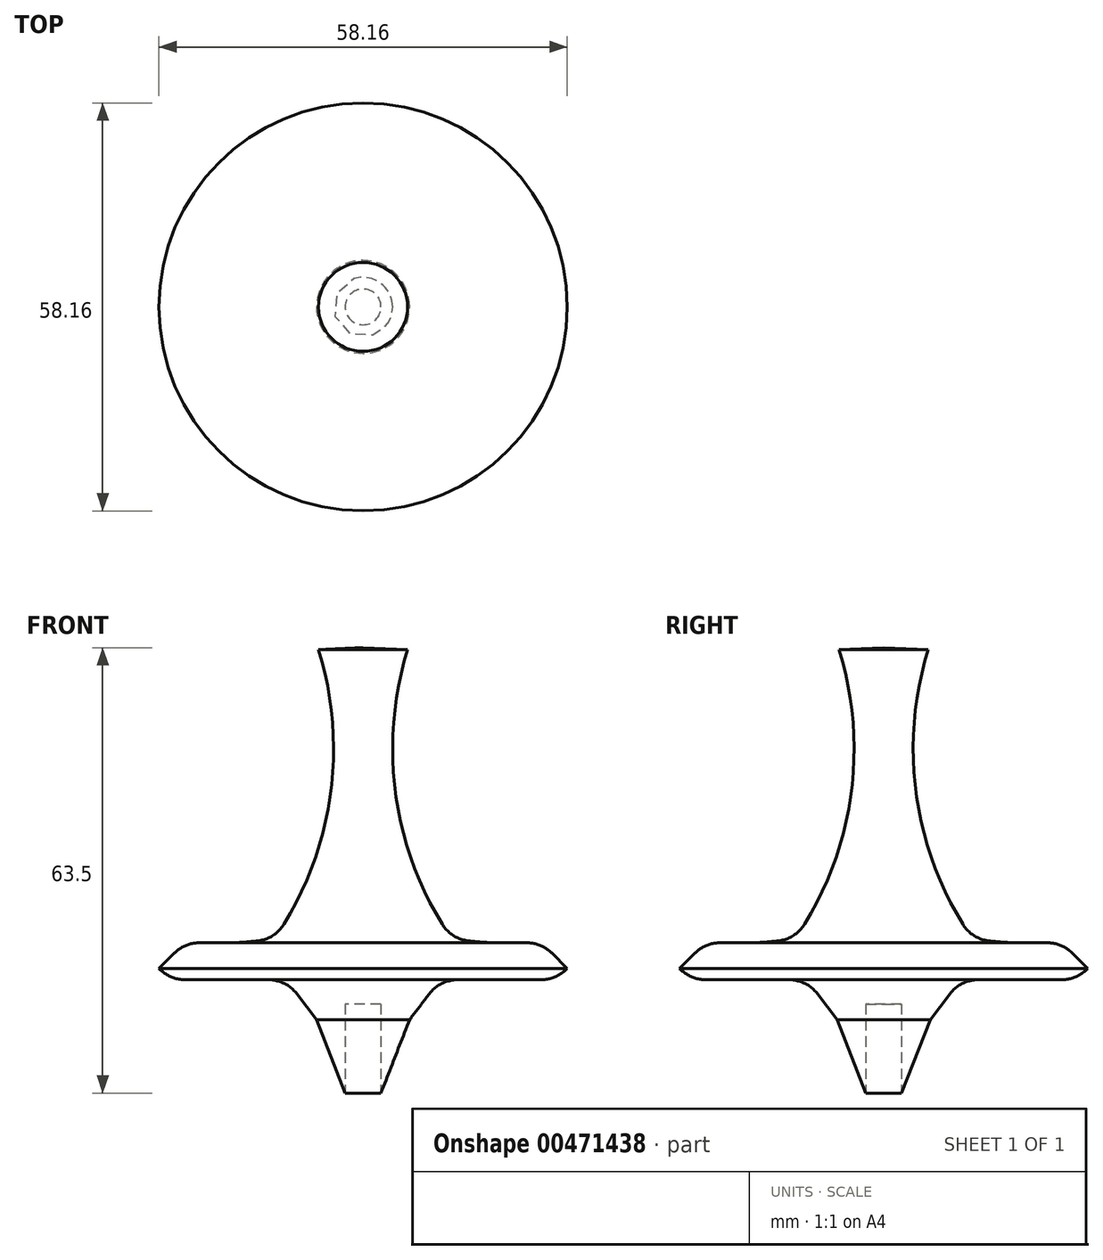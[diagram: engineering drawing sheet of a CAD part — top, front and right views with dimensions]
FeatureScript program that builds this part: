
annotation { "Feature Type Name" : "Feature", "Feature Type Description" : "" }
export const myFeature = defineFeature(function(context is Context, id is Id, definition is map)
    precondition{}
    {
        {
            var Q0;
            Q0=qCreatedBy(makeId("Front.planeOp"),FACE);
            var sketch = newSketch(context, id + "F0", { "sketchPlane" : qUnion([Q0])});
            skLineSegment(sketch, "E0", {"start": v(0, 63.5) * mm, "end": v(0, 0) * mm});
            skArc(sketch, "E1", {"start": v(12.6, 22.03) * mm, "mid": v(16.63, 21.53) * mm, "end": v(20.7, 21.42) * mm});
            skArc(sketch, "E2", {"start": v(6.34, 63.2) * mm, "mid": v(4.75, 41.9) * mm, "end": v(12.6, 22.03) * mm});
            skLineSegment(sketch, "E3", {"start": v(30.48, 16.15) * mm, "end": v(10.96, 16.15) * mm});
            skPoint(sketch, "E4.end.orphan", {"position": v(10.96, 17.31) * mm});
            skPoint(sketch, "E5", {"position": v(20.7, 21.42) * mm});
            skLineSegment(sketch, "E6", {"start": v(0, 0) * mm, "end": v(2.55, 0) * mm});
            skLineSegment(sketch, "E7", {"start": v(2.55, 0) * mm, "end": v(6.63, 10.45) * mm});
            skLineSegment(sketch, "E8", {"start": v(6.63, 10.45) * mm, "end": v(10.96, 16.15) * mm});
            skPoint(sketch, "E9.center.orphan", {"position": v(25.93, 21.42) * mm});
            skLineSegment(sketch, "E10", {"start": v(20.7, 21.42) * mm, "end": v(30.43, 21.42) * mm});
            skLineSegment(sketch, "E11", {"start": v(30.43, 21.42) * mm, "end": v(30.48, 16.15) * mm});
            skLineSegment(sketch, "E12", {"start": v(6.34, 63.2) * mm, "end": v(0, 63.5) * mm});
            skSolve(sketch);
        }
        {
            var Q0;
            Q0=qSketchRegion(id+"F0",true);
            var Q1;
            Q1=sQuery(id+"F0.wireOp",EDGE,"E0");
            revolve(context, id + "F1", {"entities" : qUnion([Q0]), "axis" : qUnion([Q1]), "revolveType" : RevolveType.FULL});
        }
        {
            var Q0;
            Q0=makeQuery(id+"F1.opRevolve","SWEPT_FACE",FACE,{"disambiguationData":[OSD([sQuery(id+"F0.wireOp",EDGE,"E6")])]});
            extrude(context, id + "F2", {"entities" : qUnion([Q0]), "operationType" : NewBodyOperationType.REMOVE, "oppositeDirection" : true, "depth" : 12.7 * mm});
        }
        {
            var Q0;
            Q0=makeQuery(id+"F1.opRevolve","SWEPT_FACE",FACE,{"disambiguationData":[OSD([sQuery(id+"F0.wireOp",EDGE,"E3")])]});
            fillet(context, id + "F3", {"entities" : qUnion([Q0]), "radius" : 5.08 * mm, "tangentPropagation" : true, "allowEdgeOverflow" : false});
        }
        {
            var Q0;
            Q0=makeQuery(id+"F1.opRevolve","SWEPT_EDGE",EDGE,{"disambiguationData":[OSD([sQuery(id+"F0.wireOp",EDGE,"E10"),sQuery(id+"F0.wireOp",EDGE,"E11")])]});
            chamfer(context, id + "F4", {"entities" : qUnion([Q0]), "width" : 5.08 * mm, "tangentPropagation" : true});
        }
        {
            var Q0;
            Q0=makeQuery(id+"F1.opRevolve","SWEPT_FACE",FACE,{"disambiguationData":[OSD([sQuery(id+"F0.wireOp",EDGE,"E1")])]});
            fillet(context, id + "F5", {"entities" : qUnion([Q0]), "radius" : 5.08 * mm, "tangentPropagation" : true, "allowEdgeOverflow" : false});
        }
        {
            var Q0;
            Q0=makeQuery(id+"F1.opRevolve","SWEPT_FACE",FACE,{"disambiguationData":[OSD([sQuery(id+"F0.wireOp",EDGE,"E10")])]});
            fillet(context, id + "F6", {"entities" : qUnion([Q0]), "radius" : 5.08 * mm, "tangentPropagation" : true, "allowEdgeOverflow" : false});
        }
    });
